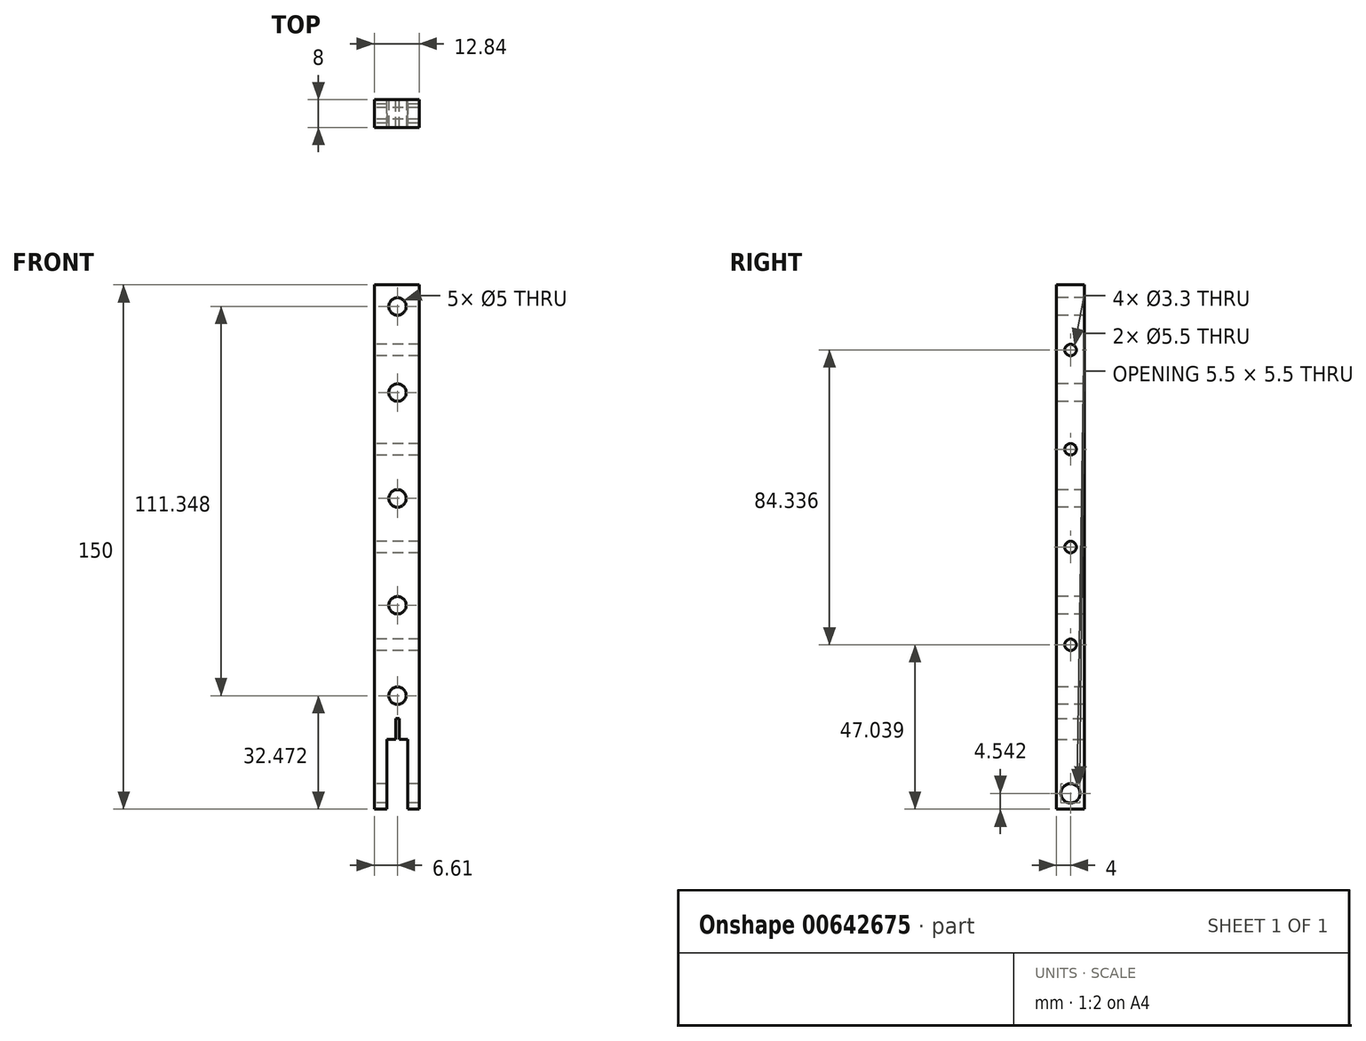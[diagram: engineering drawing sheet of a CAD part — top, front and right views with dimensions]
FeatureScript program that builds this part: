
annotation { "Feature Type Name" : "Feature", "Feature Type Description" : "" }
export const myFeature = defineFeature(function(context is Context, id is Id, definition is map)
    precondition{}
    {
        {
            var Q0;
            Q0=qCreatedBy(makeId("Front.planeOp"),FACE);
            var sketch = newSketch(context, id + "F0", { "sketchPlane" : qUnion([Q0])});
            skLineSegment(sketch, "E0", {"start": v(-3, 0) * mm, "end": v(-6.61, 0) * mm});
            skLineSegment(sketch, "E1", {"start": v(-6.61, 0) * mm, "end": v(-6.61, 150) * mm});
            skLineSegment(sketch, "E2", {"start": v(-6.61, 150) * mm, "end": v(6.23, 150) * mm});
            skLineSegment(sketch, "E3", {"start": v(6.23, 150) * mm, "end": v(6.23, 0) * mm});
            skLineSegment(sketch, "E4", {"start": v(6.23, 0) * mm, "end": v(3, 0) * mm});
            skLineSegment(sketch, "E5", {"start": v(3, 0) * mm, "end": v(3, 20) * mm});
            skLineSegment(sketch, "E6", {"start": v(3, 20) * mm, "end": v(0.5, 20) * mm});
            skLineSegment(sketch, "E7", {"start": v(0.5, 20) * mm, "end": v(0.5, 26) * mm});
            skLineSegment(sketch, "E8", {"start": v(0.5, 26) * mm, "end": v(-0.5, 26) * mm});
            skLineSegment(sketch, "E9", {"start": v(-0.5, 26) * mm, "end": v(-0.5, 20) * mm});
            skLineSegment(sketch, "E10", {"start": v(-0.5, 20) * mm, "end": v(-3, 20) * mm});
            skLineSegment(sketch, "E11", {"start": v(-3, 20) * mm, "end": v(-3, 0) * mm});
            skLineSegment(sketch, "E12", {"start": v(-0.5, 20) * mm, "end": v(0, 20) * mm, "construction": true});
            skLineSegment(sketch, "E13", {"start": v(0, 20) * mm, "end": v(0.5, 20) * mm, "construction": true});
            skSolve(sketch);
        }
        {
            var Q0;
            Q0=makeQuery(id+"F0.imprint","IMPRINT",FACE,{"disambiguationData":[TD([[makeQuery(id+"F0.imprint","IMPRINT",EDGE,{"derivedFrom":sQuery(id+"F0.wireOp",EDGE,"E0")}),-1.0]])]});
            extrude(context, id + "F1", {"entities" : qUnion([Q0]), "depth" : 8 * mm, "offsetDistance" : 25 * mm});
        }
        {
            var Q0;
            Q0=makeQuery(id+"F1.opExtrude","SWEPT_FACE",FACE,{"disambiguationData":[OSD([sQuery(id+"F0.wireOp",EDGE,"E1")])]});
            var sketch = newSketch(context, id + "F2", { "sketchPlane" : qUnion([Q0])});
            skPoint(sketch, "E14", {"position": v(4, 4.54) * mm});
            skPoint(sketch, "E14.positionSnap0", {"position": v(4, 0) * mm});
            skSolve(sketch);
        }
        {
            var Q0;
            Q0=sQuery(id+"F2.wireOp",VERTEX,"E14");
            var Q1;
            Q1=makeQuery(id+"F1.opExtrude","SWEPT_BODY",BODY,{"disambiguationData":[OSD([sQuery(id+"F0.wireOp",EDGE,"E0"),sQuery(id+"F0.wireOp",EDGE,"E1"),sQuery(id+"F0.wireOp",EDGE,"E2"),sQuery(id+"F0.wireOp",EDGE,"E3"),sQuery(id+"F0.wireOp",EDGE,"E4"),sQuery(id+"F0.wireOp",EDGE,"E5"),sQuery(id+"F0.wireOp",EDGE,"E6"),sQuery(id+"F0.wireOp",EDGE,"E7"),sQuery(id+"F0.wireOp",EDGE,"E8"),sQuery(id+"F0.wireOp",EDGE,"E9"),sQuery(id+"F0.wireOp",EDGE,"E10"),sQuery(id+"F0.wireOp",EDGE,"E11")])]});
            hole(context, id + "F3", {"style" : HoleStyle.SIMPLE, "endStyle" : HoleEndStyle.THROUGH, "holeDiameter" : 5.5 * mm, "majorDiameter" : 5 * mm, "isTappedThrough" : true, "tappedDepth" : 12 * mm, "tapClearance" : 3, "locations" : qUnion([Q0]), "scope" : qUnion([Q1])});
        }
        {
            var Q0;
            Q0=makeQuery(id+"F1.opExtrude","CAP_FACE",FACE,{"disambiguationData":[OSD([sQuery(id+"F0.wireOp",EDGE,"E0"),sQuery(id+"F0.wireOp",EDGE,"E1"),sQuery(id+"F0.wireOp",EDGE,"E2"),sQuery(id+"F0.wireOp",EDGE,"E3"),sQuery(id+"F0.wireOp",EDGE,"E4"),sQuery(id+"F0.wireOp",EDGE,"E5"),sQuery(id+"F0.wireOp",EDGE,"E6"),sQuery(id+"F0.wireOp",EDGE,"E7"),sQuery(id+"F0.wireOp",EDGE,"E8"),sQuery(id+"F0.wireOp",EDGE,"E9"),sQuery(id+"F0.wireOp",EDGE,"E10"),sQuery(id+"F0.wireOp",EDGE,"E11")])],"isStart":false});
            var sketch = newSketch(context, id + "F4", { "sketchPlane" : qUnion([Q0])});
            skLineSegment(sketch, "E15", {"start": v(0, 150) * mm, "end": v(0, 32.47) * mm, "construction": true});
            skPoint(sketch, "E16", {"position": v(0, 32.47) * mm});
            skPoint(sketch, "E17", {"position": v(0, 58.36) * mm});
            skPoint(sketch, "E18", {"position": v(0, 88.9) * mm});
            skPoint(sketch, "E19", {"position": v(0, 119.19) * mm});
            skPoint(sketch, "E20", {"position": v(0, 143.82) * mm});
            skSolve(sketch);
        }
        {
            var Q0;
            Q0=sQuery(id+"F4.wireOp",VERTEX,"E16");
            var Q1;
            Q1=sQuery(id+"F4.wireOp",VERTEX,"E17");
            var Q2;
            Q2=sQuery(id+"F4.wireOp",VERTEX,"E18");
            var Q3;
            Q3=sQuery(id+"F4.wireOp",VERTEX,"E19");
            var Q4;
            Q4=sQuery(id+"F4.wireOp",VERTEX,"E20");
            var Q5;
            Q5=makeQuery(id+"F1.opExtrude","SWEPT_BODY",BODY,{"disambiguationData":[OSD([sQuery(id+"F0.wireOp",EDGE,"E0"),sQuery(id+"F0.wireOp",EDGE,"E1"),sQuery(id+"F0.wireOp",EDGE,"E2"),sQuery(id+"F0.wireOp",EDGE,"E3"),sQuery(id+"F0.wireOp",EDGE,"E4"),sQuery(id+"F0.wireOp",EDGE,"E5"),sQuery(id+"F0.wireOp",EDGE,"E6"),sQuery(id+"F0.wireOp",EDGE,"E7"),sQuery(id+"F0.wireOp",EDGE,"E8"),sQuery(id+"F0.wireOp",EDGE,"E9"),sQuery(id+"F0.wireOp",EDGE,"E10"),sQuery(id+"F0.wireOp",EDGE,"E11")])]});
            hole(context, id + "F5", {"style" : HoleStyle.SIMPLE, "endStyle" : HoleEndStyle.THROUGH, "holeDiameter" : 5 * mm, "majorDiameter" : 5 * mm, "isTappedThrough" : true, "tappedDepth" : 12 * mm, "tapClearance" : 3, "locations" : qUnion([Q0, Q1, Q2, Q3, Q4]), "scope" : qUnion([Q5])});
        }
        {
            var Q0;
            Q0=makeQuery(id+"F1.opExtrude","SWEPT_FACE",FACE,{"disambiguationData":[OSD([sQuery(id+"F0.wireOp",EDGE,"E1")])]});
            var sketch = newSketch(context, id + "F6", { "sketchPlane" : qUnion([Q0])});
            skLineSegment(sketch, "E21", {"start": v(4, 150) * mm, "end": v(4, 0) * mm, "construction": true});
            skPoint(sketch, "E22", {"position": v(4, 131.37) * mm});
            skPoint(sketch, "E23", {"position": v(4, 102.97) * mm});
            skPoint(sketch, "E24", {"position": v(4, 75) * mm});
            skPoint(sketch, "E25", {"position": v(4, 47.04) * mm});
            skSolve(sketch);
        }
        {
            var Q0;
            Q0=sQuery(id+"F6.wireOp",VERTEX,"E22");
            var Q1;
            Q1=sQuery(id+"F6.wireOp",VERTEX,"E23");
            var Q2;
            Q2=sQuery(id+"F6.wireOp",VERTEX,"E24");
            var Q3;
            Q3=sQuery(id+"F6.wireOp",VERTEX,"E25");
            var Q4;
            Q4=makeQuery(id+"F1.opExtrude","SWEPT_BODY",BODY,{"disambiguationData":[OSD([sQuery(id+"F0.wireOp",EDGE,"E0"),sQuery(id+"F0.wireOp",EDGE,"E1"),sQuery(id+"F0.wireOp",EDGE,"E2"),sQuery(id+"F0.wireOp",EDGE,"E3"),sQuery(id+"F0.wireOp",EDGE,"E4"),sQuery(id+"F0.wireOp",EDGE,"E5"),sQuery(id+"F0.wireOp",EDGE,"E6"),sQuery(id+"F0.wireOp",EDGE,"E7"),sQuery(id+"F0.wireOp",EDGE,"E8"),sQuery(id+"F0.wireOp",EDGE,"E9"),sQuery(id+"F0.wireOp",EDGE,"E10"),sQuery(id+"F0.wireOp",EDGE,"E11")])]});
            hole(context, id + "F7", {"style" : HoleStyle.SIMPLE, "endStyle" : HoleEndStyle.THROUGH, "standardTappedOrClearance" : lookupTablePath({ "standard" : "ISO", "engagement" : "75%", "pitch" : "0.7 mm", "size" : "M4", "type" : "Tapped" }), "standardBlindInLast" : lookupTablePath({ "standard" : "ISO", "engagement" : "75%", "pitch" : "0.7 mm", "size" : "M4", "type" : "Tapped" }), "holeDiameter" : 3.3 * mm, "majorDiameter" : 4 * mm, "showTappedDepth" : true, "isTappedThrough" : true, "tappedDepth" : 12 * mm, "tapClearance" : 3, "locations" : qUnion([Q0, Q1, Q2, Q3]), "scope" : qUnion([Q4])});
        }
    });
